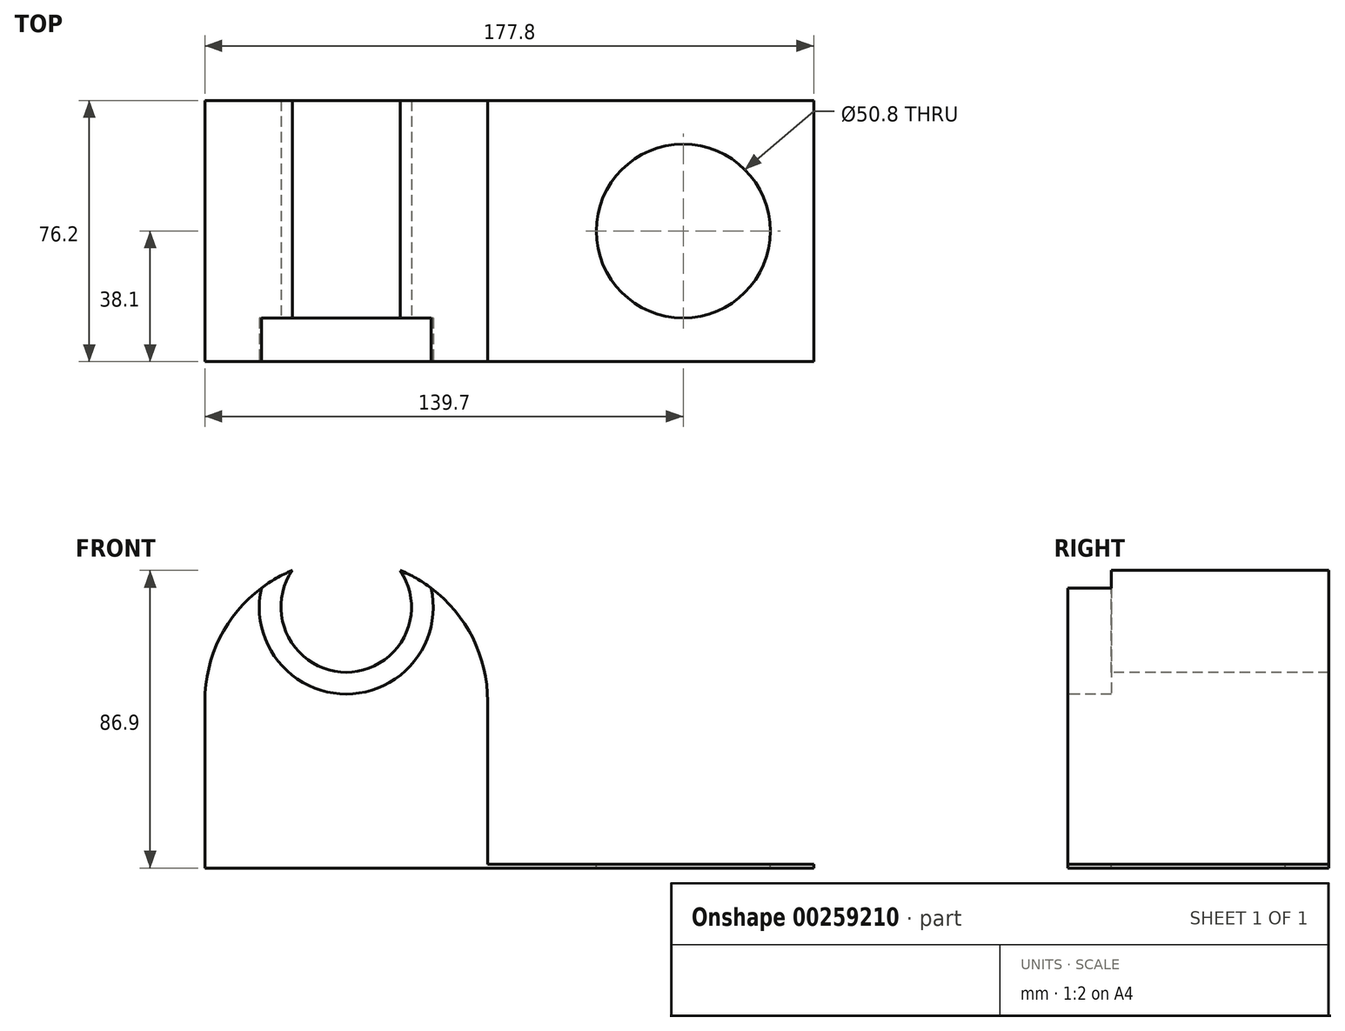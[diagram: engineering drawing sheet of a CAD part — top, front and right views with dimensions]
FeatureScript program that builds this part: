
annotation { "Feature Type Name" : "Feature", "Feature Type Description" : "" }
export const myFeature = defineFeature(function(context is Context, id is Id, definition is map)
    precondition{}
    {
        {
            var Q0;
            Q0=qCreatedBy(makeId("Top.planeOp"),FACE);
            var sketch = newSketch(context, id + "F0", { "sketchPlane" : qUnion([Q0])});
            skLineSegment(sketch, "E0.bottom", {"start": v(0, 0) * mm, "end": v(177.8, 0) * mm});
            skLineSegment(sketch, "E0.top", {"start": v(0, 76.2) * mm, "end": v(177.8, 76.2) * mm});
            skLineSegment(sketch, "E0.left", {"start": v(0, 0) * mm, "end": v(0, 76.2) * mm});
            skLineSegment(sketch, "E0.right", {"start": v(177.8, 0) * mm, "end": v(177.8, 76.2) * mm});
            skSolve(sketch);
        }
        {
            var Q0;
            Q0=makeQuery(id+"F0.imprint","IMPRINT",FACE,{"disambiguationData":[TD([[makeQuery(id+"F0.imprint","IMPRINT",EDGE,{"derivedFrom":sQuery(id+"F0.wireOp",EDGE,"E0.bottom")}),1.0]])]});
            extrude(context, id + "F1", {"entities" : qUnion([Q0]), "depth" : (1 + (1 / 8)) * mm});
        }
        {
            var Q0;
            Q0=makeQuery(id+"F1.opExtrude","CAP_FACE",FACE,{"disambiguationData":[OSD([sQuery(id+"F0.wireOp",EDGE,"E0.bottom"),sQuery(id+"F0.wireOp",EDGE,"E0.top"),sQuery(id+"F0.wireOp",EDGE,"E0.left"),sQuery(id+"F0.wireOp",EDGE,"E0.right")])],"isStart":false});
            var sketch = newSketch(context, id + "F2", { "sketchPlane" : qUnion([Q0])});
            skLineSegment(sketch, "E1.bottom", {"start": v(0, 0) * mm, "end": v(82.55, 0) * mm});
            skLineSegment(sketch, "E1.top", {"start": v(0, 76.2) * mm, "end": v(82.55, 76.2) * mm});
            skLineSegment(sketch, "E1.left", {"start": v(0, 0) * mm, "end": v(0, 76.2) * mm});
            skLineSegment(sketch, "E1.right", {"start": v(82.55, 0) * mm, "end": v(82.55, 76.2) * mm});
            skSolve(sketch);
        }
        {
            var Q0;
            Q0=makeQuery(id+"F2.imprint","IMPRINT",FACE,{"disambiguationData":[TD([[makeQuery(id+"F2.imprint","IMPRINT",EDGE,{"derivedFrom":sQuery(id+"F2.wireOp",EDGE,"E1.bottom")}),1.0]])]});
            extrude(context, id + "F3", {"entities" : qUnion([Q0]), "operationType" : NewBodyOperationType.ADD, "depth" : 88.9 * mm});
        }
        {
            var Q0;
            Q0=makeQuery(id+"F3.opExtrude","CAP_EDGE",EDGE,{"disambiguationData":[OSD([sQuery(id+"F2.wireOp",EDGE,"E1.right")])],"isStart":false});
            var Q1;
            Q1=makeQuery(id+"F3.opExtrude","CAP_EDGE",EDGE,{"disambiguationData":[OSD([sQuery(id+"F2.wireOp",EDGE,"E1.left")])],"isStart":false});
            fillet(context, id + "F4", {"entities" : qUnion([Q0, Q1]), "radius" : 41.27 * mm, "tangentPropagation" : true, "allowEdgeOverflow" : false});
        }
        {
            var Q0;
            Q0=makeQuery(id+"F3.boolean.opBoolean","MERGE",FACE,{"derivedFrom":[makeQuery(id+"F1.opExtrude","SWEPT_FACE",FACE,{"disambiguationData":[OSD([sQuery(id+"F0.wireOp",EDGE,"E0.bottom")])]}),makeQuery(id+"F3.opExtrude","SWEPT_FACE",FACE,{"disambiguationData":[OSD([sQuery(id+"F2.wireOp",EDGE,"E1.bottom")])]})]});
            var sketch = newSketch(context, id + "F5", { "sketchPlane" : qUnion([Q0])});
            skCircle(sketch, "E2", {"center": v(41.27, 76.2) * mm, "radius": 19.05 * mm});
            skSolve(sketch);
        }
        {
            var Q0;
            Q0=makeQuery(id+"F5.imprint","IMPRINT",FACE,{"disambiguationData":[TD([[makeQuery(id+"F5.imprint","IMPRINT",EDGE,{"derivedFrom":sQuery(id+"F5.wireOp",EDGE,"E2")}),1.0]])]});
            extrude(context, id + "F6", {"entities" : qUnion([Q0]), "operationType" : NewBodyOperationType.REMOVE, "oppositeDirection" : true, "depth" : 101.6 * mm});
        }
        {
            var Q0;
            Q0=makeQuery(id+"F3.boolean.opBoolean","MERGE",FACE,{"derivedFrom":[makeQuery(id+"F1.opExtrude","SWEPT_FACE",FACE,{"disambiguationData":[OSD([sQuery(id+"F0.wireOp",EDGE,"E0.bottom")])]}),makeQuery(id+"F3.opExtrude","SWEPT_FACE",FACE,{"disambiguationData":[OSD([sQuery(id+"F2.wireOp",EDGE,"E1.bottom")])]})]});
            var sketch = newSketch(context, id + "F7", { "sketchPlane" : qUnion([Q0])});
            skCircle(sketch, "E3", {"center": v(41.27, 76.2) * mm, "radius": 25.4 * mm});
            skSolve(sketch);
        }
        {
            var Q0;
            Q0=makeQuery(id+"F7.imprint","IMPRINT",FACE,{"disambiguationData":[TD([[makeQuery(id+"F7.imprint","IMPRINT",EDGE,{"derivedFrom":sQuery(id+"F7.wireOp",EDGE,"E3")}),1.0]])]});
            extrude(context, id + "F8", {"entities" : qUnion([Q0]), "operationType" : NewBodyOperationType.REMOVE, "oppositeDirection" : true, "depth" : 12.7 * mm});
        }
        {
            var Q0;
            Q0=makeQuery(id+"F1.opExtrude","CAP_FACE",FACE,{"disambiguationData":[OSD([sQuery(id+"F0.wireOp",EDGE,"E0.bottom"),sQuery(id+"F0.wireOp",EDGE,"E0.top"),sQuery(id+"F0.wireOp",EDGE,"E0.left"),sQuery(id+"F0.wireOp",EDGE,"E0.right")])],"isStart":false});
            var sketch = newSketch(context, id + "F9", { "sketchPlane" : qUnion([Q0])});
            skLineSegment(sketch, "E4", {"start": v(177.8, 0) * mm, "end": v(177.8, 38.1) * mm});
            skLineSegment(sketch, "E5", {"start": v(177.8, 38.1) * mm, "end": v(139.7, 38.1) * mm});
            skCircle(sketch, "E6", {"center": v(139.7, 38.1) * mm, "radius": 25.4 * mm});
            skCircle(sketch, "E7", {"center": v(139.7, 38.1) * mm, "radius": 19.05 * mm});
            skSolve(sketch);
        }
        {
            var Q0;
            Q0=makeQuery(id+"F9.imprint","IMPRINT",FACE,{"disambiguationData":[TD([[makeQuery(id+"F9.imprint","IMPRINT",EDGE,{"derivedFrom":sQuery(id+"F9.wireOp",EDGE,"E7")}),1.0]])]});
            extrude(context, id + "F10", {"entities" : qUnion([Q0]), "operationType" : NewBodyOperationType.REMOVE, "oppositeDirection" : true, "depth" : 50.8 * mm});
        }
        {
            var Q0;
            Q0=makeQuery(id+"F9.imprint","IMPRINT",FACE,{"disambiguationData":[TD([[makeQuery(id+"F9.imprint","IMPRINT",EDGE,{"derivedFrom":sQuery(id+"F9.wireOp",EDGE,"E6")}),1.0]])]});
            extrude(context, id + "F11", {"entities" : qUnion([Q0]), "operationType" : NewBodyOperationType.REMOVE, "oppositeDirection" : true, "depth" : 12.7 * mm});
        }
    });
